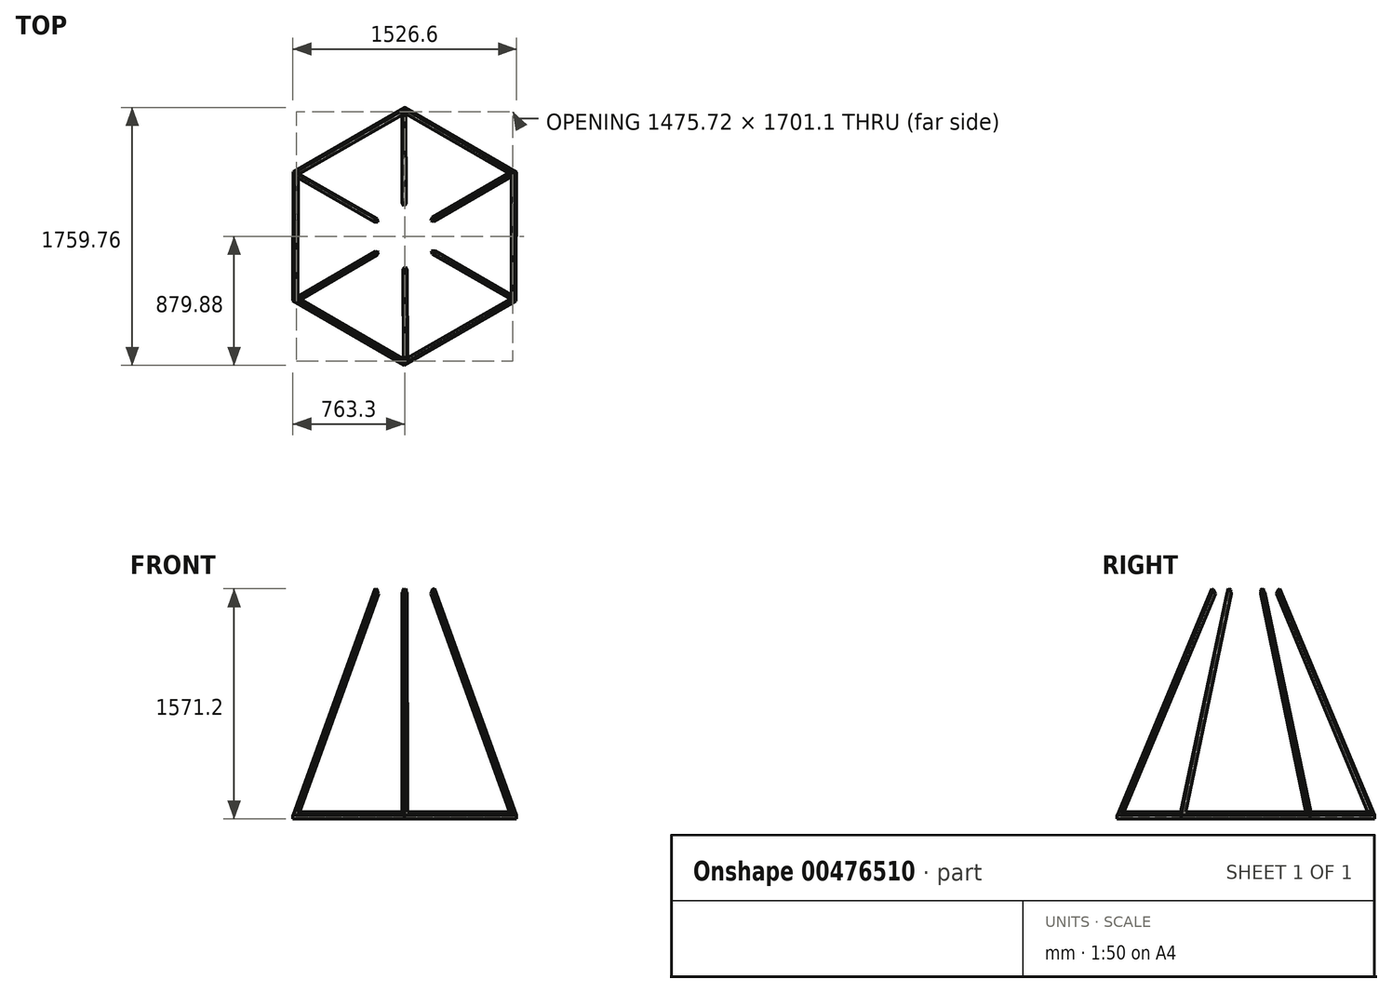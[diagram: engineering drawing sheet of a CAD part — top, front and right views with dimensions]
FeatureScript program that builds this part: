
annotation { "Feature Type Name" : "Feature", "Feature Type Description" : "" }
export const myFeature = defineFeature(function(context is Context, id is Id, definition is map)
    precondition{}
    {
        {
            var Q0;
            Q0=qCreatedBy(makeId("Top.planeOp"),FACE);
            var sketch = newSketch(context, id + "F0", { "sketchPlane" : qUnion([Q0])});
            skCircle(sketch, "E0.cCircle", {"center": v(0, 0) * mm, "radius": 762 * mm, "construction": true});
            skLineSegment(sketch, "E0.0", {"start": v(2.61, 879.88) * mm, "end": v(763.3, 437.68) * mm});
            skLineSegment(sketch, "E0.1", {"start": v(763.3, 437.68) * mm, "end": v(760.7, -442.2) * mm});
            skLineSegment(sketch, "E0.2", {"start": v(760.7, -442.2) * mm, "end": v(-2.61, -879.88) * mm});
            skLineSegment(sketch, "E0.3", {"start": v(-2.61, -879.88) * mm, "end": v(-763.3, -437.68) * mm});
            skLineSegment(sketch, "E0.4", {"start": v(-763.3, -437.68) * mm, "end": v(-760.7, 442.2) * mm});
            skLineSegment(sketch, "E0.5", {"start": v(-760.7, 442.2) * mm, "end": v(2.61, 879.88) * mm});
            skPoint(sketch, "E0.0.midPoint", {"position": v(382.96, 658.78) * mm});
            skLineSegment(sketch, "E1.0", {"start": v(-737.86, -423.09) * mm, "end": v(-735.34, 427.46) * mm});
            skLineSegment(sketch, "E1.1", {"start": v(2.52, 850.55) * mm, "end": v(737.86, 423.09) * mm});
            skLineSegment(sketch, "E1.2", {"start": v(737.86, 423.09) * mm, "end": v(735.34, -427.46) * mm});
            skLineSegment(sketch, "E1.3", {"start": v(-735.34, 427.46) * mm, "end": v(2.52, 850.55) * mm});
            skLineSegment(sketch, "E1.4", {"start": v(735.34, -427.46) * mm, "end": v(-2.52, -850.55) * mm});
            skLineSegment(sketch, "E1.5", {"start": v(-2.52, -850.55) * mm, "end": v(-737.86, -423.09) * mm});
            skLineSegment(sketch, "E2", {"start": v(-735.34, 427.46) * mm, "end": v(-760.7, 442.2) * mm});
            skLineSegment(sketch, "E3", {"start": v(-737.86, -423.09) * mm, "end": v(-763.3, -437.68) * mm});
            skLineSegment(sketch, "E4", {"start": v(-2.52, -850.55) * mm, "end": v(-2.61, -879.88) * mm});
            skLineSegment(sketch, "E5", {"start": v(760.7, -442.2) * mm, "end": v(735.34, -427.46) * mm});
            skLineSegment(sketch, "E6", {"start": v(763.3, 437.68) * mm, "end": v(737.86, 423.09) * mm});
            skLineSegment(sketch, "E7", {"start": v(2.61, 879.88) * mm, "end": v(2.52, 850.55) * mm});
            skSolve(sketch);
        }
        {
            var Q0;
            Q0 = qSketchRegion(id + "F0", true);
            extrude(context, id + "F1", {"entities" : qUnion([Q0]), "depth" : 25.4 * mm});
        }
        {
            var Q0;
            Q0=qCreatedBy(makeId("Top.planeOp"),FACE);
            cPlane(context, id + "F2", {"entities" : qUnion([Q0]), "cplaneType" : CPlaneType.OFFSET, "offset" : 25.4 * mm, "width" : 152.4 * mm, "height" : 152.4 * mm});
        }
        {
            var Q0;
            Q0=makeQuery(id+"F1.opExtrude","SWEPT_FACE",FACE,{"disambiguationData":[OSD([sQuery(id+"F0.wireOp",EDGE,"E0.4")])]});
            var Q1;
            Q1=makeQuery(id+"F1.opExtrude","CAP_EDGE",EDGE,{"disambiguationData":[OSD([sQuery(id+"F0.wireOp",EDGE,"E1.0")])],"isStart":false});
            cPlane(context, id + "F3", {"entities" : qUnion([Q0, Q1]), "cplaneType" : CPlaneType.LINE_ANGLE, "offset" : 25.4 * mm, "angle" : 20 * degree, "width" : 152.4 * mm, "height" : 152.4 * mm});
        }
        {
            var Q0;
            Q0=qCreatedBy(id+"F3.planeOp",FACE);
            cPlane(context, id + "F4", {"entities" : qUnion([Q0]), "cplaneType" : CPlaneType.OFFSET, "offset" : 22.25 * mm, "oppositeDirection" : true, "width" : 152.4 * mm, "height" : 152.4 * mm});
        }
        {
            var Q0;
            Q0=qCreatedBy(id+"F4.planeOp",FACE);
            var sketch = newSketch(context, id + "F5", { "sketchPlane" : qUnion([Q0])});
            skLineSegment(sketch, "E8", {"start": v(440.18, -236.3) * mm, "end": v(118.64, 1408.97) * mm});
            skLineSegment(sketch, "E9", {"start": v(440.18, -236.3) * mm, "end": v(-439.7, -237.2) * mm});
            skLineSegment(sketch, "E10.2", {"start": v(409.34, -210.94) * mm, "end": v(97.72, 1383.57) * mm});
            skLineSegment(sketch, "E10.3", {"start": v(409.34, -210.94) * mm, "end": v(-408.94, -211.77) * mm});
            skLineSegment(sketch, "E11", {"start": v(97.72, 1383.57) * mm, "end": v(118.64, 1408.97) * mm});
            skLineSegment(sketch, "E12", {"start": v(-408.94, -211.77) * mm, "end": v(-439.7, -237.2) * mm});
            skLineSegment(sketch, "E13", {"start": v(409.34, -210.94) * mm, "end": v(440.18, -236.3) * mm});
            skSolve(sketch);
        }
        {
            var Q0;
            Q0=qCreatedBy(makeId("Front.planeOp"),FACE);
            var sketch = newSketch(context, id + "F6", { "sketchPlane" : qUnion([Q0])});
            skLineSegment(sketch, "E14", {"start": v(0, -65.83) * mm, "end": v(0, 79.74) * mm});
            skSolve(sketch);
        }
        {
            var Q0;
            Q0=makeQuery(id+"F5.imprint","IMPRINT",FACE,{"disambiguationData":[TD([[makeQuery(id+"F5.imprint","IMPRINT",EDGE,{"derivedFrom":sQuery(id+"F5.wireOp",EDGE,"VAvZ2E9I-rWMZ-TXWX-nndm-AR0kGcHmUA8e")}),1.0]])]});
            var Q1;
            Q1=makeQuery(id+"F5.imprint","IMPRINT",FACE,{"disambiguationData":[TD([[makeQuery(id+"F5.imprint","IMPRINT",EDGE,{"derivedFrom":sQuery(id+"F5.wireOp",EDGE,"jcZJ9U8S-6T8G-Nooe-gjKj-oBDwU0c2aoEQ")}),1.0]])]});
            var Q2;
            Q2=makeQuery(id+"F5.imprint","IMPRINT",FACE,{"disambiguationData":[TD([[makeQuery(id+"F5.imprint","IMPRINT",EDGE,{"derivedFrom":sQuery(id+"F5.wireOp",EDGE,"E8")}),1.0]])]});
            var Q3;
            Q3=makeQuery(id+"F5.imprint","IMPRINT",FACE,{"disambiguationData":[TD([[makeQuery(id+"F5.imprint","IMPRINT",EDGE,{"derivedFrom":sQuery(id+"F5.wireOp",EDGE,"3d22324a-b27c-4cfb-8239-88b9c9b5c1ab.2")}),-1.0]])]});
            var Q4;
            Q4=makeQuery(id+"F5.imprint","IMPRINT",FACE,{"disambiguationData":[TD([[makeQuery(id+"F5.imprint","IMPRINT",EDGE,{"derivedFrom":sQuery(id+"F5.wireOp",EDGE,"E9")}),-1.0]])]});
            extrude(context, id + "F7", {"entities" : qUnion([Q0, Q1, Q2, Q3, Q4]), "depth" : 25.4 * mm});
        }
        {
            var Q0;
            Q0=makeQuery(id+"F1.opExtrude","SWEPT_BODY",BODY,{"disambiguationData":[OSD([sQuery(id+"F0.wireOp",EDGE,"E0.0"),sQuery(id+"F0.wireOp",EDGE,"E0.1"),sQuery(id+"F0.wireOp",EDGE,"E0.2"),sQuery(id+"F0.wireOp",EDGE,"E0.3"),sQuery(id+"F0.wireOp",EDGE,"E0.4"),sQuery(id+"F0.wireOp",EDGE,"E0.5"),sQuery(id+"F0.wireOp",EDGE,"E1.0"),sQuery(id+"F0.wireOp",EDGE,"E1.1"),sQuery(id+"F0.wireOp",EDGE,"E1.2"),sQuery(id+"F0.wireOp",EDGE,"E1.3"),sQuery(id+"F0.wireOp",EDGE,"E1.4"),sQuery(id+"F0.wireOp",EDGE,"E1.5")])]});
            var Q1;
            Q1=makeQuery(id+"F7.opExtrude","SWEPT_BODY",BODY,{"disambiguationData":[OSD([sQuery(id+"F5.wireOp",EDGE,"E8"),sQuery(id+"F5.wireOp",EDGE,"VAvZ2E9I-rWMZ-TXWX-nndm-AR0kGcHmUA8e"),sQuery(id+"F5.wireOp",EDGE,"jcZJ9U8S-6T8G-Nooe-gjKj-oBDwU0c2aoEQ"),sQuery(id+"F5.wireOp",EDGE,"3d22324a-b27c-4cfb-8239-88b9c9b5c1ab.0"),sQuery(id+"F5.wireOp",EDGE,"3d22324a-b27c-4cfb-8239-88b9c9b5c1ab.1"),sQuery(id+"F5.wireOp",EDGE,"3d22324a-b27c-4cfb-8239-88b9c9b5c1ab.2"),sQuery(id+"F5.wireOp",EDGE,"3d22324a-b27c-4cfb-8239-88b9c9b5c1ab.3"),sQuery(id+"F5.wireOp",EDGE,"E9")])]});
            booleanBodies(context, id + "F8", {"operationType" : BooleanOperationType.SUBTRACTION, "tools" : qUnion([Q0]), "targets" : qUnion([Q1]), "keepTools" : true});
        }
        {
            var Q0;
            Q0=makeQuery(id+"F7.opExtrude","CAP_EDGE",EDGE,{"disambiguationData":[OSD([sQuery(id+"F5.wireOp",EDGE,"E8")])],"isStart":false});
            var Q1;
            Q1=makeQuery(id+"F7.opExtrude","CAP_EDGE",EDGE,{"disambiguationData":[OSD([sQuery(id+"F5.wireOp",EDGE,"jcZJ9U8S-6T8G-Nooe-gjKj-oBDwU0c2aoEQ")])],"isStart":false});
            chamfer(context, id + "F9", {"entities" : qUnion([Q0, Q1]), "chamferType" : ChamferType.OFFSET_ANGLE, "width" : 25.4 * mm, "oppositeDirection" : false, "angle" : 30 * degree, "tangentPropagation" : true});
        }
        {
            var Q0;
            Q0=makeQuery(id+"F7.opExtrude","SWEPT_BODY",BODY,{"disambiguationData":[OSD([sQuery(id+"F5.wireOp",EDGE,"E8"),sQuery(id+"F5.wireOp",EDGE,"VAvZ2E9I-rWMZ-TXWX-nndm-AR0kGcHmUA8e"),sQuery(id+"F5.wireOp",EDGE,"jcZJ9U8S-6T8G-Nooe-gjKj-oBDwU0c2aoEQ"),sQuery(id+"F5.wireOp",EDGE,"3d22324a-b27c-4cfb-8239-88b9c9b5c1ab.0"),sQuery(id+"F5.wireOp",EDGE,"3d22324a-b27c-4cfb-8239-88b9c9b5c1ab.1"),sQuery(id+"F5.wireOp",EDGE,"3d22324a-b27c-4cfb-8239-88b9c9b5c1ab.2"),sQuery(id+"F5.wireOp",EDGE,"3d22324a-b27c-4cfb-8239-88b9c9b5c1ab.3"),sQuery(id+"F5.wireOp",EDGE,"E9")])]});
            var Q1;
            Q1=sQuery(id+"F6.wireOp",EDGE,"E14");
            circularPattern(context, id + "F10", {"entities" : qUnion([Q0]), "axis" : qUnion([Q1]), "angle" : 360 * degree, "instanceCount" : 6, "equalSpace" : true});
        }
    });
